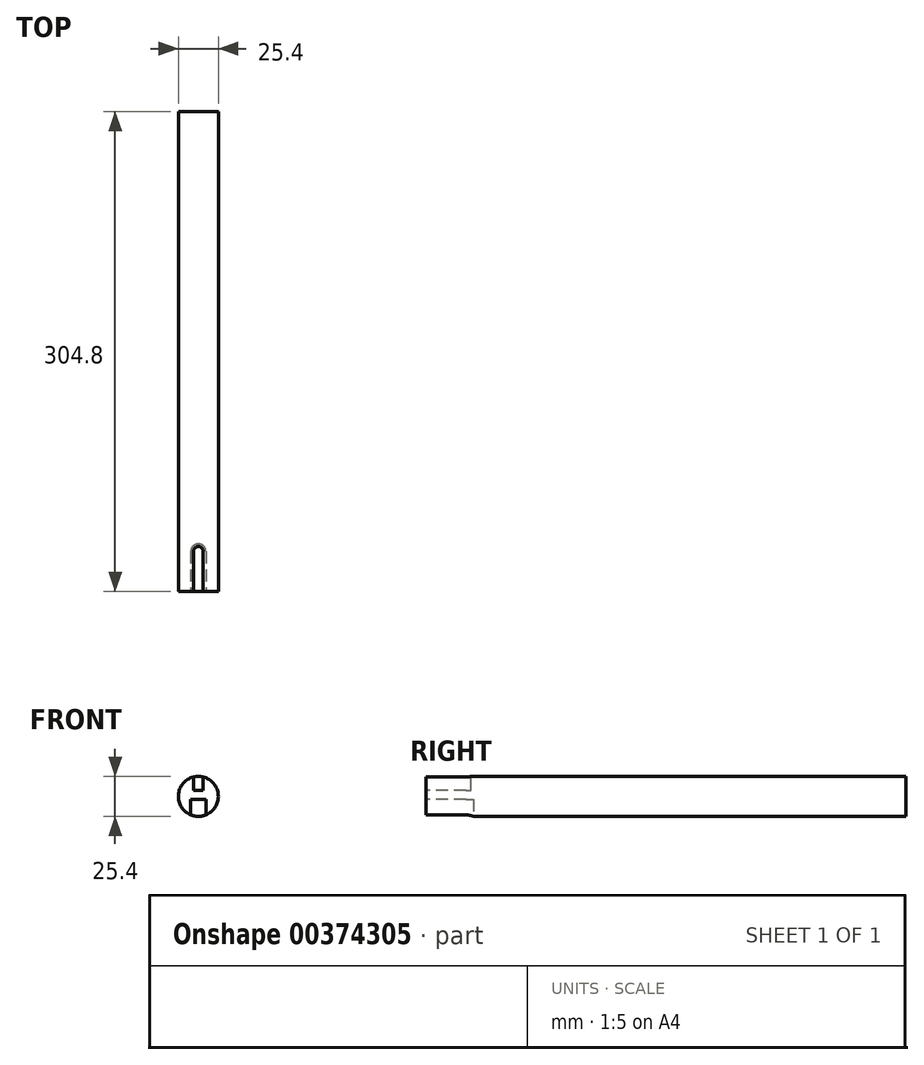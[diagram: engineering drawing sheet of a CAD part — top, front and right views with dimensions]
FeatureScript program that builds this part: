
annotation { "Feature Type Name" : "Feature", "Feature Type Description" : "" }
export const myFeature = defineFeature(function(context is Context, id is Id, definition is map)
    precondition{}
    {
        {
            var Q0;
            Q0=qCreatedBy(makeId("Front.planeOp"),FACE);
            var sketch = newSketch(context, id + "F0", { "sketchPlane" : qUnion([Q0])});
            skCircle(sketch, "E0", {"center": v(0, 0) * mm, "radius": 12.7 * mm});
            skSolve(sketch);
        }
        {
            var Q0;
            Q0 = qSketchRegion(id + "F0", true);
            extrude(context, id + "F1", {"entities" : qUnion([Q0]), "oppositeDirection" : true, "depth" : 304.8 * mm});
        }
        {
            var Q0;
            Q0=makeQuery(id+"F1.opExtrude","CAP_FACE",FACE,{"disambiguationData":[OSD([sQuery(id+"F0.wireOp",EDGE,"E0")])],"isStart":true});
            var sketch = newSketch(context, id + "F2", { "sketchPlane" : qUnion([Q0])});
            skArc(sketch, "E1.0", {"start": v(-4.76, -11.77) * mm, "mid": v(0, -12.7) * mm, "end": v(4.76, -11.77) * mm});
            skLineSegment(sketch, "E2.bottom", {"start": v(-4.76, -1.9) * mm, "end": v(4.76, -1.9) * mm});
            skLineSegment(sketch, "E2.left", {"start": v(-4.76, -1.9) * mm, "end": v(-4.76, -11.77) * mm});
            skLineSegment(sketch, "E2.right", {"start": v(4.76, -1.9) * mm, "end": v(4.76, -11.77) * mm});
            skLineSegment(sketch, "E3.bottom", {"start": v(-3.17, 3.8) * mm, "end": v(3.18, 3.8) * mm});
            skLineSegment(sketch, "E3.left", {"start": v(-3.17, 3.8) * mm, "end": v(-3.18, 12.3) * mm});
            skLineSegment(sketch, "E3.right", {"start": v(3.18, 3.8) * mm, "end": v(3.17, 12.3) * mm});
            skArc(sketch, "E4.trimOffspring", {"start": v(3.17, 12.3) * mm, "mid": v(0, 12.7) * mm, "end": v(-3.17, 12.3) * mm});
            skSolve(sketch);
        }
        {
            var Q0;
            Q0=makeQuery(id+"F2.imprint","IMPRINT",FACE,{"disambiguationData":[TD([[makeQuery(id+"F2.imprint","IMPRINT",EDGE,{"derivedFrom":sQuery(id+"F2.wireOp",EDGE,"E3.bottom")}),1.0]])]});
            var Q1;
            Q1=makeQuery(id+"F2.imprint","IMPRINT",FACE,{"disambiguationData":[TD([[makeQuery(id+"F2.imprint","IMPRINT",EDGE,{"derivedFrom":sQuery(id+"F2.wireOp",EDGE,"E2.bottom")}),-1.0]])]});
            extrude(context, id + "F3", {"entities" : qUnion([Q0, Q1]), "operationType" : NewBodyOperationType.REMOVE, "oppositeDirection" : true, "depth" : 25.4 * mm});
        }
        {
            var Q0;
            Q0=qCreatedBy(makeId("Top.planeOp"),FACE);
            cPlane(context, id + "F4", {"entities" : qUnion([Q0]), "cplaneType" : CPlaneType.OFFSET, "offset" : 12.7 * mm, "width" : 152.4 * mm, "height" : 152.4 * mm});
        }
        {
            var Q0;
            Q0=qCreatedBy(makeId("Top.planeOp"),FACE);
            cPlane(context, id + "F5", {"entities" : qUnion([Q0]), "cplaneType" : CPlaneType.OFFSET, "offset" : 12.7 * mm, "oppositeDirection" : true, "width" : 152.4 * mm, "height" : 152.4 * mm});
        }
        {
            var Q0;
            Q0=qCreatedBy(id+"F4.planeOp",FACE);
            var sketch = newSketch(context, id + "F6", { "sketchPlane" : qUnion([Q0])});
            skLineSegment(sketch, "E5.0", {"start": v(3.18, 25.4) * mm, "end": v(-3.18, 25.4) * mm});
            skCircle(sketch, "E6", {"center": v(0, 25.4) * mm, "radius": 3.18 * mm});
            skSolve(sketch);
        }
        {
            var Q0;
            {var subQ0=sQuery(id+"F6.wireOp",EDGE,"E5.0");Q0=makeQuery(id+"F6.imprint","IMPRINT",FACE,{"disambiguationData":[TD([[makeQuery(id+"F6.imprint","IMPRINT",EDGE,{"derivedFrom":subQ0}),-1.0]])]});}
            var Q1;
            Q1=makeQuery(id+"F3.boolean.opBoolean","COPY",FACE,{"derivedFrom":makeQuery(id+"F3.opExtrude","SWEPT_FACE",FACE,{"disambiguationData":[OSD([sQuery(id+"F2.wireOp",EDGE,"E3.bottom")])]})});
            extrude(context, id + "F7", {"entities" : qUnion([Q0]), "operationType" : NewBodyOperationType.REMOVE, "endBound" : BoundingType.UP_TO_SURFACE, "oppositeDirection" : true, "endBoundEntityFace" : qUnion([Q1]), "depth" : 25.4 * mm});
        }
        {
            var Q0;
            Q0=qCreatedBy(id+"F5.planeOp",FACE);
            var sketch = newSketch(context, id + "F8", { "sketchPlane" : qUnion([Q0])});
            skLineSegment(sketch, "E7.0", {"start": v(-4.76, 25.4) * mm, "end": v(4.76, 25.4) * mm});
            skCircle(sketch, "E8", {"center": v(0, 25.4) * mm, "radius": 4.76 * mm});
            skSolve(sketch);
        }
        {
            var Q0;
            {var subQ0=sQuery(id+"F8.wireOp",EDGE,"E7.0");Q0=makeQuery(id+"F8.imprint","IMPRINT",FACE,{"disambiguationData":[TD([[makeQuery(id+"F8.imprint","IMPRINT",EDGE,{"derivedFrom":subQ0}),1.0]])]});}
            var Q1;
            Q1=makeQuery(id+"F3.boolean.opBoolean","COPY",FACE,{"derivedFrom":makeQuery(id+"F3.opExtrude","SWEPT_FACE",FACE,{"disambiguationData":[OSD([sQuery(id+"F2.wireOp",EDGE,"E2.bottom")])]})});
            extrude(context, id + "F9", {"entities" : qUnion([Q0]), "operationType" : NewBodyOperationType.REMOVE, "endBound" : BoundingType.UP_TO_SURFACE, "endBoundEntityFace" : qUnion([Q1]), "depth" : 25.4 * mm});
        }
    });
